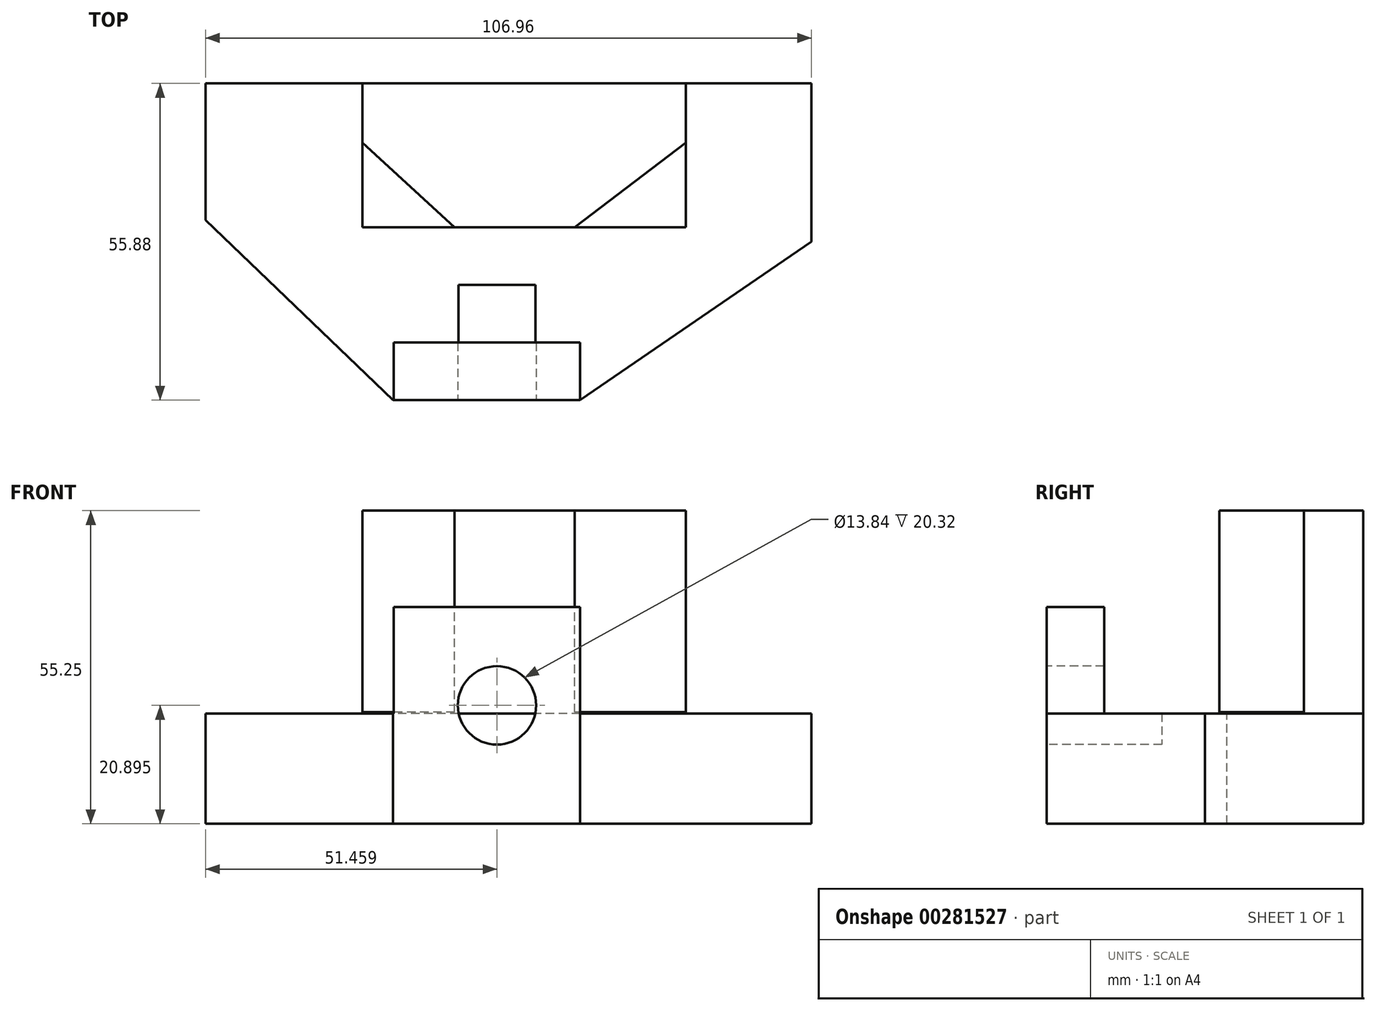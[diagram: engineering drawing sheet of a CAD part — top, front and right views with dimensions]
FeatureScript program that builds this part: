
annotation { "Feature Type Name" : "Feature", "Feature Type Description" : "" }
export const myFeature = defineFeature(function(context is Context, id is Id, definition is map)
    precondition{}
    {
        {
            var Q0;
            Q0=qCreatedBy(makeId("Front.planeOp"),FACE);
            var sketch = newSketch(context, id + "F0", { "sketchPlane" : qUnion([Q0])});
            skLineSegment(sketch, "E0.bottom", {"start": v(45.5, 11.84) * mm, "end": v(-61.46, 11.84) * mm});
            skLineSegment(sketch, "E0.top", {"start": v(45.5, -7.64) * mm, "end": v(-61.46, -7.64) * mm});
            skLineSegment(sketch, "E0.left", {"start": v(45.5, 11.84) * mm, "end": v(45.5, -7.64) * mm});
            skLineSegment(sketch, "E0.right", {"start": v(-61.46, 11.84) * mm, "end": v(-61.46, -7.64) * mm});
            skSolve(sketch);
        }
        {
            var Q0;
            Q0=makeQuery(id+"F0.imprint","IMPRINT",FACE,{"disambiguationData":[TD([[makeQuery(id+"F0.imprint","IMPRINT",EDGE,{"derivedFrom":sQuery(id+"F0.wireOp",EDGE,"E0.bottom")}),1.0]])]});
            extrude(context, id + "F1", {"entities" : qUnion([Q0]), "depth" : 55.88 * mm});
        }
        {
            var Q0;
            Q0=makeQuery(id+"F1.opExtrude","SWEPT_FACE",FACE,{"disambiguationData":[OSD([sQuery(id+"F0.wireOp",EDGE,"E0.bottom")])]});
            var sketch = newSketch(context, id + "F2", { "sketchPlane" : qUnion([Q0])});
            skLineSegment(sketch, "E1", {"start": v(4.7, -55.88) * mm, "end": v(45.5, -27.94) * mm});
            skLineSegment(sketch, "E2", {"start": v(-28.38, -55.88) * mm, "end": v(-61.46, -24.1) * mm});
            skSolve(sketch);
        }
        {
            var Q0;
            {var subQ0=sQuery(id+"F2.wireOp",EDGE,"E1");Q0=makeQuery(id+"F2.imprint","IMPRINT",FACE,{"disambiguationData":[TD([[makeQuery(id+"F2.imprint","IMPRINT",EDGE,{"derivedFrom":subQ0}),-1.0]])]});}
            var Q1;
            {var subQ0=sQuery(id+"F2.wireOp",EDGE,"E2");Q1=makeQuery(id+"F2.imprint","IMPRINT",FACE,{"disambiguationData":[TD([[makeQuery(id+"F2.imprint","IMPRINT",EDGE,{"derivedFrom":subQ0}),1.0]])]});}
            extrude(context, id + "F3", {"entities" : qUnion([Q0, Q1]), "operationType" : NewBodyOperationType.REMOVE, "oppositeDirection" : true, "depth" : 25.4 * mm});
        }
        {
            var Q0;
            Q0=qCreatedBy(makeId("Front.planeOp"),FACE);
            var sketch = newSketch(context, id + "F4", { "sketchPlane" : qUnion([Q0])});
            skLineSegment(sketch, "E3.bottom", {"start": v(23.34, 11.75) * mm, "end": v(-33.75, 11.75) * mm});
            skLineSegment(sketch, "E3.top", {"start": v(23.34, 47.61) * mm, "end": v(-33.75, 47.61) * mm});
            skLineSegment(sketch, "E3.left", {"start": v(23.34, 11.75) * mm, "end": v(23.34, 47.61) * mm});
            skLineSegment(sketch, "E3.right", {"start": v(-33.75, 11.75) * mm, "end": v(-33.75, 47.61) * mm});
            skSolve(sketch);
        }
        {
            var Q0;
            Q0=makeQuery(id+"F4.imprint","IMPRINT",FACE,{"disambiguationData":[TD([[makeQuery(id+"F4.imprint","IMPRINT",EDGE,{"derivedFrom":sQuery(id+"F4.wireOp",EDGE,"E3.bottom")}),-1.0]])]});
            extrude(context, id + "F5", {"entities" : qUnion([Q0]), "operationType" : NewBodyOperationType.ADD, "depth" : 25.4 * mm});
        }
        {
            var Q0;
            Q0=makeQuery(id+"F5.opExtrude","SWEPT_FACE",FACE,{"disambiguationData":[OSD([sQuery(id+"F4.wireOp",EDGE,"E3.top")])]});
            var sketch = newSketch(context, id + "F6", { "sketchPlane" : qUnion([Q0])});
            skLineSegment(sketch, "E4", {"start": v(3.7, -25.4) * mm, "end": v(23.34, -10.5) * mm});
            skLineSegment(sketch, "E5", {"start": v(-17.46, -25.4) * mm, "end": v(-33.75, -10.5) * mm});
            skSolve(sketch);
        }
        {
            var Q0;
            {var subQ0=sQuery(id+"F6.wireOp",EDGE,"E4");Q0=makeQuery(id+"F6.imprint","IMPRINT",FACE,{"disambiguationData":[TD([[makeQuery(id+"F6.imprint","IMPRINT",EDGE,{"derivedFrom":subQ0}),-1.0]])]});}
            var Q1;
            {var subQ0=sQuery(id+"F6.wireOp",EDGE,"E5");Q1=makeQuery(id+"F6.imprint","IMPRINT",FACE,{"disambiguationData":[TD([[makeQuery(id+"F6.imprint","IMPRINT",EDGE,{"derivedFrom":subQ0}),1.0]])]});}
            extrude(context, id + "F7", {"entities" : qUnion([Q0, Q1]), "operationType" : NewBodyOperationType.REMOVE, "oppositeDirection" : true, "depth" : 35.56 * mm});
        }
        {
            var Q0;
            Q0=makeQuery(id+"F1.opExtrude","CAP_FACE",FACE,{"disambiguationData":[OSD([sQuery(id+"F0.wireOp",EDGE,"E0.bottom"),sQuery(id+"F0.wireOp",EDGE,"E0.top"),sQuery(id+"F0.wireOp",EDGE,"E0.left"),sQuery(id+"F0.wireOp",EDGE,"E0.right")])],"isStart":false});
            var sketch = newSketch(context, id + "F8", { "sketchPlane" : qUnion([Q0])});
            skLineSegment(sketch, "E6.bottom", {"start": v(4.7, -7.64) * mm, "end": v(-28.2, -7.64) * mm});
            skLineSegment(sketch, "E6.top", {"start": v(4.7, 30.6) * mm, "end": v(-28.2, 30.6) * mm});
            skLineSegment(sketch, "E6.left", {"start": v(4.7, -7.64) * mm, "end": v(4.7, 30.6) * mm});
            skLineSegment(sketch, "E6.right", {"start": v(-28.2, -7.64) * mm, "end": v(-28.2, 30.6) * mm});
            skSolve(sketch);
        }
        {
            var Q0;
            {var subQ0=sQuery(id+"F8.wireOp",EDGE,"E6.top");Q0=makeQuery(id+"F8.imprint","IMPRINT",FACE,{"disambiguationData":[TD([[makeQuery(id+"F8.imprint","IMPRINT",EDGE,{"derivedFrom":subQ0}),1.0]])]});}
            extrude(context, id + "F9", {"entities" : qUnion([Q0]), "operationType" : NewBodyOperationType.ADD, "oppositeDirection" : true, "depth" : 10.16 * mm});
        }
        {
            var Q0;
            {var subQ0=sQuery(id+"F0.wireOp",EDGE,"E0.bottom");Q0=makeQuery(id+"F9.boolean.opBoolean","MERGE",FACE,{"derivedFrom":[makeQuery(id+"F1.opExtrude","CAP_FACE",FACE,{"disambiguationData":[OSD([subQ0,sQuery(id+"F0.wireOp",EDGE,"E0.top"),sQuery(id+"F0.wireOp",EDGE,"E0.left"),sQuery(id+"F0.wireOp",EDGE,"E0.right")])],"isStart":false}),makeQuery(id+"F9.opExtrude","CAP_FACE",FACE,{"disambiguationData":[OSD([subQ0,sQuery(id+"F8.wireOp",EDGE,"E6.top"),sQuery(id+"F8.wireOp",EDGE,"E6.left"),sQuery(id+"F8.wireOp",EDGE,"E6.right")])],"isStart":true})]});}
            var sketch = newSketch(context, id + "F10", { "sketchPlane" : qUnion([Q0])});
            skLineSegment(sketch, "E7", {"start": v(-10, 13.26) * mm, "end": v(-8.5, 30.6) * mm});
            skLineSegment(sketch, "E8", {"start": v(-10, 13.26) * mm, "end": v(-25.44, 14.6) * mm});
            skLineSegment(sketch, "E9", {"start": v(-10, 13.26) * mm, "end": v(-10, -1.94) * mm});
            skLineSegment(sketch, "E10", {"start": v(-10, 13.26) * mm, "end": v(2.93, 13.26) * mm});
            skCircle(sketch, "E11", {"center": v(-10, 13.26) * mm, "radius": 6.92 * mm});
            skSolve(sketch);
        }
        {
            var Q0;
            {var subQ1=sQuery(id+"F10.wireOp",EDGE,"E9");var subQ3=sQuery(id+"F10.wireOp",EDGE,"E11");var subQ4=makeQuery(id+"F10.imprint","INTERSECT",VERTEX,{"derivedFrom":[subQ1,subQ3]});Q0=makeQuery(id+"F10.imprint","IMPRINT",FACE,{"disambiguationData":[TD([[makeQuery(id+"F10.imprint","IMPRINT",EDGE,{"disambiguationData":[TD([[subQ4,-1.0]])],"derivedFrom":subQ3}),1.0]])]});}
            var Q1;
            {var subQ1=sQuery(id+"F10.wireOp",EDGE,"E8");var subQ3=sQuery(id+"F10.wireOp",EDGE,"E11");var subQ4=makeQuery(id+"F10.imprint","INTERSECT",VERTEX,{"derivedFrom":[subQ1,subQ3]});Q1=makeQuery(id+"F10.imprint","IMPRINT",FACE,{"disambiguationData":[TD([[makeQuery(id+"F10.imprint","IMPRINT",EDGE,{"disambiguationData":[TD([[subQ4,-1.0]])],"derivedFrom":subQ3}),1.0]])]});}
            var Q2;
            {var subQ1=sQuery(id+"F10.wireOp",EDGE,"E7");var subQ3=sQuery(id+"F10.wireOp",EDGE,"E11");var subQ4=makeQuery(id+"F10.imprint","INTERSECT",VERTEX,{"derivedFrom":[subQ1,subQ3]});Q2=makeQuery(id+"F10.imprint","IMPRINT",FACE,{"disambiguationData":[TD([[makeQuery(id+"F10.imprint","IMPRINT",EDGE,{"disambiguationData":[TD([[subQ4,-1.0]])],"derivedFrom":subQ3}),1.0]])]});}
            var Q3;
            {var subQ1=sQuery(id+"F10.wireOp",EDGE,"E7");var subQ3=sQuery(id+"F10.wireOp",EDGE,"E11");var subQ4=makeQuery(id+"F10.imprint","INTERSECT",VERTEX,{"derivedFrom":[subQ1,subQ3]});Q3=makeQuery(id+"F10.imprint","IMPRINT",FACE,{"disambiguationData":[TD([[makeQuery(id+"F10.imprint","IMPRINT",EDGE,{"disambiguationData":[TD([[subQ4,1.0]])],"derivedFrom":subQ3}),1.0]])]});}
            extrude(context, id + "F11", {"entities" : qUnion([Q0, Q1, Q2, Q3]), "operationType" : NewBodyOperationType.REMOVE, "oppositeDirection" : true, "depth" : 20.32 * mm});
        }
    });
